# Revit family: QF_MACOM_RGM_FCM-1000
name_source: partatom
category: Specialty Equipment
units: mm (PartAtom-declared; Revit-internal decimal feet)

## family parameters
Always vertical = Yes
Cut with Voids When Loaded = No
OmniClass Number = 23.40.40.11.11
OmniClass Title = Refrigerators and Freezers
Part Type = Normal
Room Calculation Point = No
Round Connector Dimension = Use Diameter
Shared = No
Work Plane-Based = No

## types (2) — shared parameters
Capacity in Liters = 228,0 L
Climate Class = 5
Cycle = 60 Hz
Default Elevation = 0,00 mm
Depth = 660,00 mm
Drain Size = 1/2"
Elec Connection Height = 100,00 mm
Electric Power = 338 W
Height = 940,00 mm
Ingress Protection Code = IP 22
Manufacturer = MACOM
Operational Current = 2 A
Refrigerant Type = R134a
Refrigeration Defrost Drain = Yes
URL = https://www.acosmacom.com.br
Volts = 220 V
Volume = 0,62 m³
Weight = 84,00 kg
Width = 1000,00 mm

## per-type parameters (varying)
| type | Description | Work Temperature |
| FCM-1000 | FREEZER HORIZONTAL PORTATÍL - PARA COPOS | De -20ºC a -10ºC |
| RGM-1000 | REFRIGERADOR HORIZONTAL PARA GARRAFAS MACOM-1000X660X960 | De -5ºC a 6ºC |

note: column(s) folded — value = type name in every type: Model

## geometry (parser evidence)
native form markers: Sweep x9
no freeform markers — native parametric forms only
